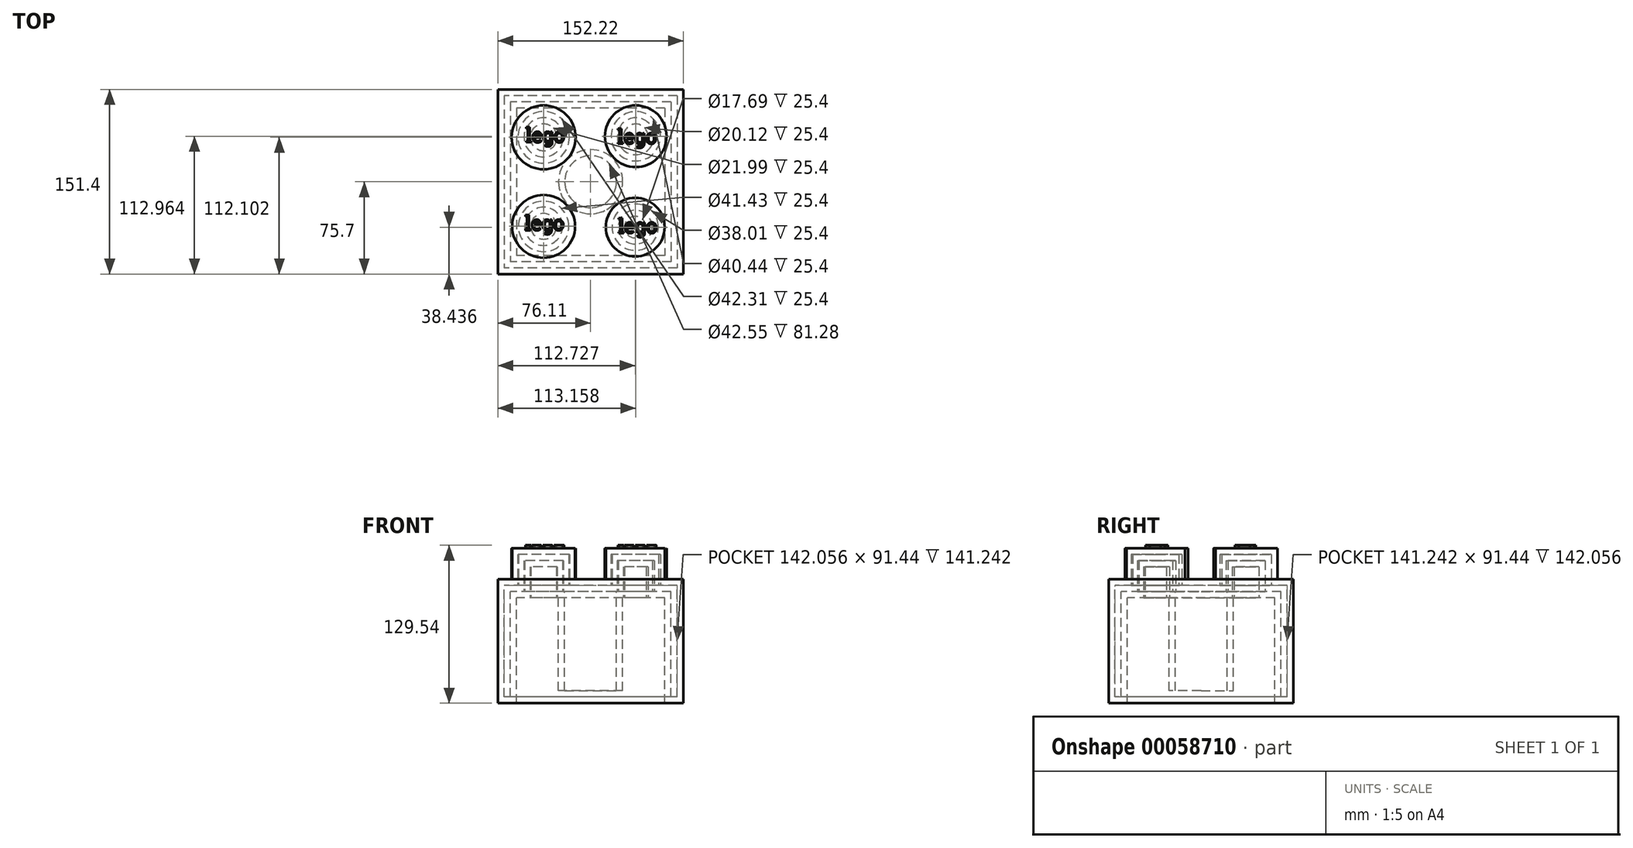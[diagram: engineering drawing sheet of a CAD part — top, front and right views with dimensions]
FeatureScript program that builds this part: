
annotation { "Feature Type Name" : "Feature", "Feature Type Description" : "" }
export const myFeature = defineFeature(function(context is Context, id is Id, definition is map)
    precondition{}
    {
        {
            var Q0;
            Q0=qCreatedBy(makeId("Top.planeOp"),FACE);
            var sketch = newSketch(context, id + "F0", { "sketchPlane" : qUnion([Q0])});
            skLineSegment(sketch, "E0.rect.bottom", {"start": v(76.1, 75.7) * mm, "end": v(-76.1, 75.7) * mm});
            skLineSegment(sketch, "E0.rect.top", {"start": v(76.1, -75.7) * mm, "end": v(-76.1, -75.7) * mm});
            skLineSegment(sketch, "E0.rect.left", {"start": v(76.1, 75.7) * mm, "end": v(76.1, -75.7) * mm});
            skLineSegment(sketch, "E0.rect.right", {"start": v(-76.1, 75.7) * mm, "end": v(-76.1, -75.7) * mm});
            skPoint(sketch, "E0.rect.middle", {"position": v(0, 0) * mm});
            skSolve(sketch);
        }
        {
            var Q0;
            Q0=makeQuery(id+"F0.imprint","IMPRINT",FACE,{"disambiguationData":[TD([[makeQuery(id+"F0.imprint","IMPRINT",EDGE,{"derivedFrom":sQuery(id+"F0.wireOp",EDGE,"E0.rect.bottom")}),1.0]])]});
            extrude(context, id + "F1", {"entities" : qUnion([Q0]), "oppositeDirection" : true, "depth" : 101.6 * mm});
        }
        {
            var Q0;
            Q0=makeQuery(id+"F1.opExtrude","CAP_FACE",FACE,{"disambiguationData":[OSD([sQuery(id+"F0.wireOp",EDGE,"E0.rect.bottom"),sQuery(id+"F0.wireOp",EDGE,"E0.rect.top"),sQuery(id+"F0.wireOp",EDGE,"E0.rect.left"),sQuery(id+"F0.wireOp",EDGE,"E0.rect.right")])],"isStart":true});
            var sketch = newSketch(context, id + "F2", { "sketchPlane" : qUnion([Q0])});
            skCircle(sketch, "E1", {"center": v(-38.56, 36.4) * mm, "radius": 26.24 * mm});
            skSolve(sketch);
        }
        {
            var Q0;
            Q0=makeQuery(id+"F2.imprint","IMPRINT",FACE,{"disambiguationData":[TD([[makeQuery(id+"F2.imprint","IMPRINT",EDGE,{"derivedFrom":sQuery(id+"F2.wireOp",EDGE,"E1")}),-1.0]])]});
            var sketch = newSketch(context, id + "F3", { "sketchPlane" : qUnion([Q0])});
            skCircle(sketch, "E2", {"center": v(37.05, 37.26) * mm, "radius": 25.3 * mm});
            skSolve(sketch);
        }
        {
            var Q0;
            Q0=makeQuery(id+"F2.imprint","IMPRINT",FACE,{"disambiguationData":[TD([[makeQuery(id+"F2.imprint","IMPRINT",EDGE,{"derivedFrom":sQuery(id+"F2.wireOp",EDGE,"E1")}),-1.0]])]});
            var sketch = newSketch(context, id + "F4", { "sketchPlane" : qUnion([Q0])});
            skCircle(sketch, "E3", {"center": v(-38.56, -36.62) * mm, "radius": 25.8 * mm});
            skSolve(sketch);
        }
        {
            var Q0;
            Q0=makeQuery(id+"F4.imprint","IMPRINT",FACE,{"disambiguationData":[TD([[makeQuery(id+"F4.imprint","IMPRINT",EDGE,{"derivedFrom":sQuery(id+"F4.wireOp",EDGE,"E3")}),-1.0]])]});
            var sketch = newSketch(context, id + "F5", { "sketchPlane" : qUnion([Q0])});
            skCircle(sketch, "E4", {"center": v(36.62, -37.26) * mm, "radius": 24.09 * mm});
            skSolve(sketch);
        }
        {
            var Q0;
            Q0=makeQuery(id+"F4.imprint","IMPRINT",FACE,{"disambiguationData":[TD([[makeQuery(id+"F4.imprint","IMPRINT",EDGE,{"derivedFrom":sQuery(id+"F4.wireOp",EDGE,"E3")}),1.0]])]});
            extrude(context, id + "F6", {"entities" : qUnion([Q0]), "operationType" : NewBodyOperationType.ADD, "depth" : 25.4 * mm});
        }
        {
            var Q0;
            Q0=makeQuery(id+"F5.imprint","IMPRINT",FACE,{"disambiguationData":[TD([[makeQuery(id+"F5.imprint","IMPRINT",EDGE,{"derivedFrom":sQuery(id+"F5.wireOp",EDGE,"E4")}),1.0]])]});
            extrude(context, id + "F7", {"entities" : qUnion([Q0]), "operationType" : NewBodyOperationType.ADD, "depth" : 25.4 * mm});
        }
        {
            var Q0;
            Q0=makeQuery(id+"F3.imprint","IMPRINT",FACE,{"disambiguationData":[TD([[makeQuery(id+"F3.imprint","IMPRINT",EDGE,{"derivedFrom":sQuery(id+"F3.wireOp",EDGE,"E2")}),1.0]])]});
            extrude(context, id + "F8", {"entities" : qUnion([Q0]), "operationType" : NewBodyOperationType.ADD, "depth" : 25.4 * mm});
        }
        {
            var Q0;
            Q0=makeQuery(id+"F2.imprint","IMPRINT",FACE,{"disambiguationData":[TD([[makeQuery(id+"F2.imprint","IMPRINT",EDGE,{"derivedFrom":sQuery(id+"F2.wireOp",EDGE,"E1")}),1.0]])]});
            extrude(context, id + "F9", {"entities" : qUnion([Q0]), "operationType" : NewBodyOperationType.ADD, "depth" : 25.4 * mm});
        }
        {
            var Q0;
            Q0=makeQuery(id+"F1.opExtrude","CAP_FACE",FACE,{"disambiguationData":[OSD([sQuery(id+"F0.wireOp",EDGE,"E0.rect.bottom"),sQuery(id+"F0.wireOp",EDGE,"E0.rect.top"),sQuery(id+"F0.wireOp",EDGE,"E0.rect.left"),sQuery(id+"F0.wireOp",EDGE,"E0.rect.right")])],"isStart":false});
            shell(context, id + "F10", {"entities" : qUnion([Q0]), "thickness" : 15.24 * mm});
        }
        {
            var Q0;
            Q0=makeQuery(id+"F10.opShell","OFFSET_FACE",FACE,{"disambiguationData":[OSD([sQuery(id+"F0.wireOp",EDGE,"E0.rect.bottom"),sQuery(id+"F0.wireOp",EDGE,"E0.rect.top"),sQuery(id+"F0.wireOp",EDGE,"E0.rect.left"),sQuery(id+"F0.wireOp",EDGE,"E0.rect.right")])]});
            var sketch = newSketch(context, id + "F11", { "sketchPlane" : qUnion([Q0])});
            skCircle(sketch, "E5", {"center": v(0, 0) * mm, "radius": 26.36 * mm});
            skSolve(sketch);
        }
        {
            var Q0;
            Q0=makeQuery(id+"F11.imprint","IMPRINT",FACE,{"disambiguationData":[TD([[makeQuery(id+"F11.imprint","IMPRINT",EDGE,{"derivedFrom":sQuery(id+"F11.wireOp",EDGE,"E5")}),1.0]])]});
            extrude(context, id + "F12", {"entities" : qUnion([Q0]), "operationType" : NewBodyOperationType.ADD, "depth" : 76.2 * mm});
        }
        {
            var Q0;
            Q0=makeQuery(id+"F12.opExtrude","CAP_FACE",FACE,{"disambiguationData":[OSD([sQuery(id+"F11.wireOp",EDGE,"E5")])],"isStart":false});
            shell(context, id + "F13", {"entities" : qUnion([Q0]), "thickness" : 5.08 * mm});
        }
        {
            var Q0;
            Q0=makeQuery(id+"F6.opExtrude","CAP_FACE",FACE,{"disambiguationData":[OSD([sQuery(id+"F4.wireOp",EDGE,"E3")])],"isStart":false});
            var sketch = newSketch(context, id + "F14", { "sketchPlane" : qUnion([Q0])});
            skText(sketch, "E6", { "text": "lego", "fontName": "RobotoSlab-Regular.ttf"});
            const initialGuessF14  = {"E6": [-0.0539, -0.03982, 1, 0, 0.01173]};
            skSetInitialGuess(sketch, initialGuessF14);
            skSolve(sketch);
        }
        {
            var Q0;
            Q0 = qSketchRegion(id + "F14", true);
            extrude(context, id + "F15", {"entities" : qUnion([Q0]), "operationType" : NewBodyOperationType.ADD, "depth" : 2.54 * mm});
        }
        {
            var Q0;
            Q0=makeQuery(id+"F7.opExtrude","CAP_FACE",FACE,{"disambiguationData":[OSD([sQuery(id+"F5.wireOp",EDGE,"E4")])],"isStart":false});
            var sketch = newSketch(context, id + "F16", { "sketchPlane" : qUnion([Q0])});
            skText(sketch, "E7", { "text": "lego", "fontName": "RobotoSlab-Regular.ttf"});
            const initialGuessF16  = {"E7": [0.0224, -0.0421, 1, 0, 0.01173]};
            skSetInitialGuess(sketch, initialGuessF16);
            skSolve(sketch);
        }
        {
            var Q0;
            Q0 = qSketchRegion(id + "F16", true);
            extrude(context, id + "F17", {"entities" : qUnion([Q0]), "operationType" : NewBodyOperationType.ADD, "depth" : 2.54 * mm});
        }
        {
            var Q0;
            Q0=makeQuery(id+"F9.opExtrude","CAP_FACE",FACE,{"disambiguationData":[OSD([sQuery(id+"F2.wireOp",EDGE,"E1")])],"isStart":false});
            var sketch = newSketch(context, id + "F18", { "sketchPlane" : qUnion([Q0])});
            skText(sketch, "E8", { "text": "lego", "fontName": "RobotoSlab-Regular.ttf"});
            const initialGuessF18  = {"E8": [0.02203, 0.03116, 1, 0, 0.01173]};
            skSetInitialGuess(sketch, initialGuessF18);
            skSolve(sketch);
        }
        {
            var Q0;
            Q0=makeQuery(id+"F8.opExtrude","CAP_FACE",FACE,{"disambiguationData":[OSD([sQuery(id+"F3.wireOp",EDGE,"E2")])],"isStart":false});
            var sketch = newSketch(context, id + "F19", { "sketchPlane" : qUnion([Q0])});
            skText(sketch, "E9", { "text": "lego", "fontName": "RobotoSlab-Regular.ttf"});
            const initialGuessF19  = {"E9": [-0.0534, 0.0323, 1, 0, 0.01173]};
            skSetInitialGuess(sketch, initialGuessF19);
            skSolve(sketch);
        }
        {
            var Q0;
            Q0 = qSketchRegion(id + "F18", true);
            var Q1;
            Q1 = qSketchRegion(id + "F19", true);
            extrude(context, id + "F20", {"entities" : qUnion([Q0, Q1]), "operationType" : NewBodyOperationType.ADD, "depth" : 2.54 * mm});
        }
    });
